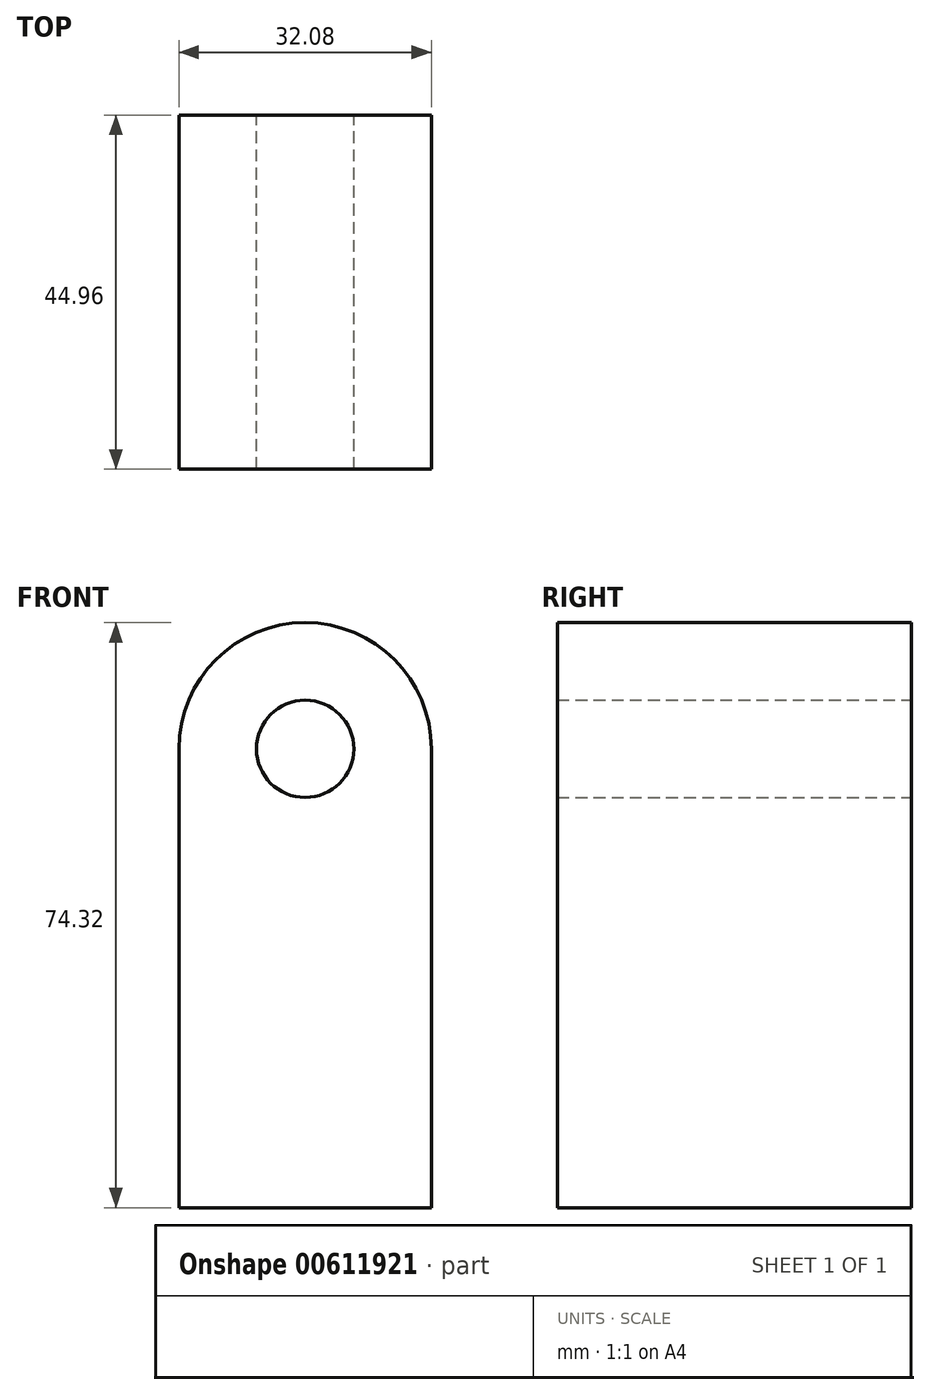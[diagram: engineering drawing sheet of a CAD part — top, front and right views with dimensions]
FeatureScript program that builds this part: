
annotation { "Feature Type Name" : "Feature", "Feature Type Description" : "" }
export const myFeature = defineFeature(function(context is Context, id is Id, definition is map)
    precondition{}
    {
        {
            var Q0;
            Q0=qCreatedBy(makeId("Front.planeOp"),FACE);
            var sketch = newSketch(context, id + "F0", { "sketchPlane" : qUnion([Q0])});
            skLineSegment(sketch, "E0.top", {"start": v(-16.04, -29.14) * mm, "end": v(16.04, -29.14) * mm});
            skLineSegment(sketch, "E0.left", {"start": v(-16.04, 29.14) * mm, "end": v(-16.04, -29.14) * mm});
            skLineSegment(sketch, "E0.right", {"start": v(16.04, 29.14) * mm, "end": v(16.04, -29.14) * mm});
            skPoint(sketch, "E0.middle", {"position": v(0, 0) * mm});
            skArc(sketch, "E1", {"start": v(16.04, 29.14) * mm, "mid": v(0, 45.18) * mm, "end": v(-16.04, 29.14) * mm});
            skCircle(sketch, "E2", {"center": v(0, 29.14) * mm, "radius": 6.18 * mm});
            skSolve(sketch);
        }
        {
            var Q0;
            Q0 = qSketchRegion(id + "F0", true);
            extrude(context, id + "F1", {"entities" : qUnion([Q0]), "depth" : 44.96 * mm, "offsetDistance" : 25.4 * mm});
        }
    });
